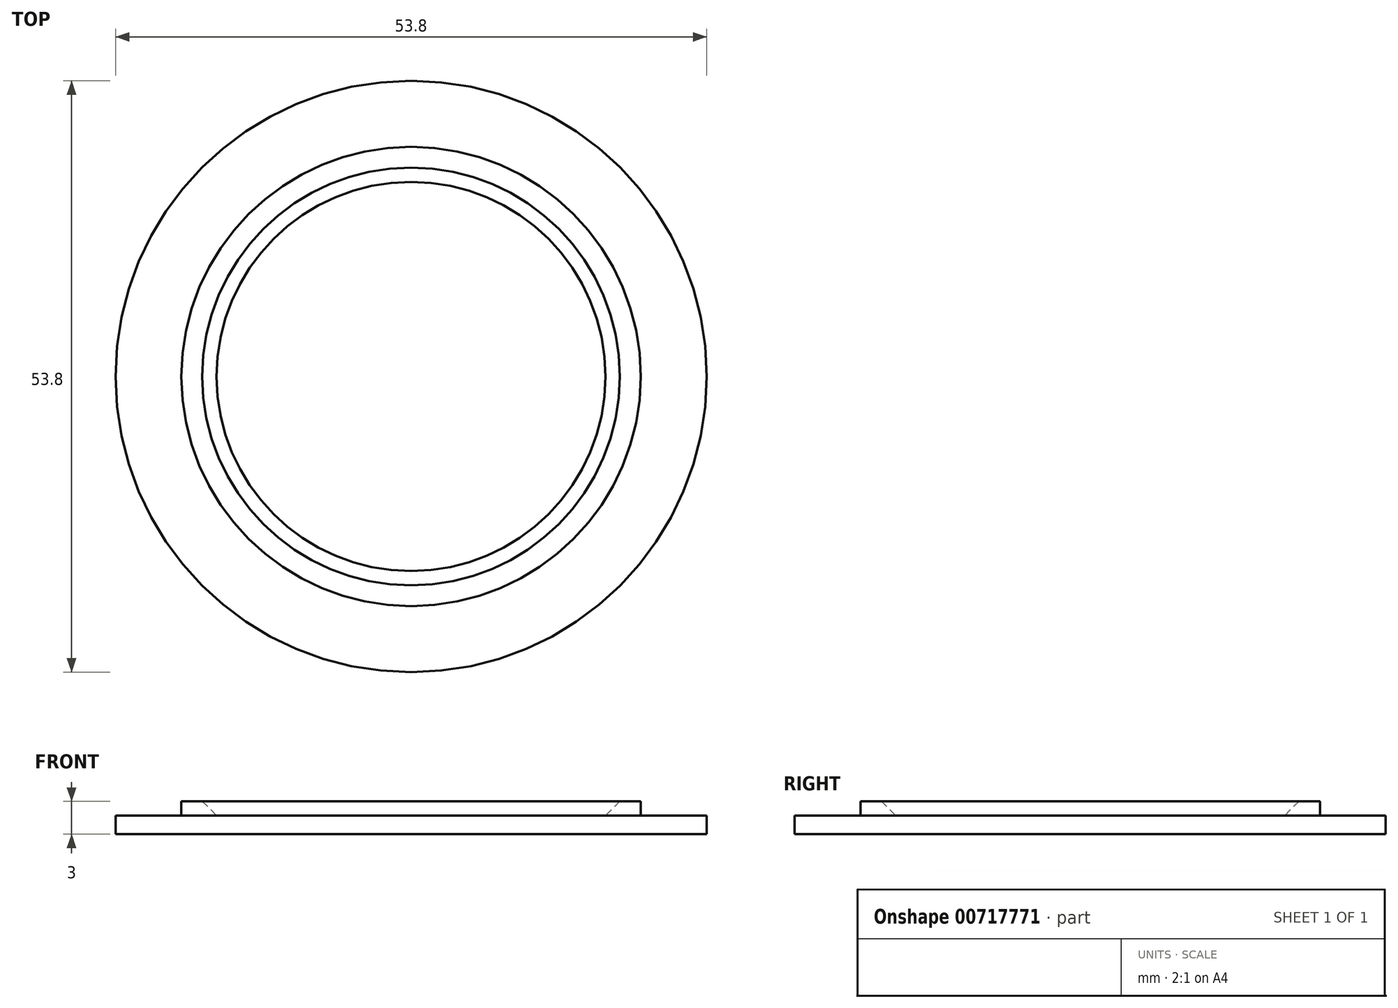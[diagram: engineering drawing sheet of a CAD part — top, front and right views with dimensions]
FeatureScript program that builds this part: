
annotation { "Feature Type Name" : "Feature", "Feature Type Description" : "" }
export const myFeature = defineFeature(function(context is Context, id is Id, definition is map)
    precondition{}
    {
        {
            var Q0;
            Q0=qCreatedBy(makeId("Top.planeOp"),FACE);
            var sketch = newSketch(context, id + "F0", { "sketchPlane" : qUnion([Q0])});
            skCircle(sketch, "E0", {"center": v(0, 0) * mm, "radius": 26.9 * mm});
            skCircle(sketch, "E1", {"center": v(0, 0) * mm, "radius": 20.9 * mm});
            skSolve(sketch);
        }
        {
            var Q0;
            Q0 = qSketchRegion(id + "F0", true);
            extrude(context, id + "F1", {"entities" : qUnion([Q0]), "depth" : 1.7 * mm, "offsetDistance" : 25 * mm});
        }
        {
            var Q0;
            Q0=makeQuery(id+"F0.imprint","IMPRINT",FACE,{"disambiguationData":[TD([[makeQuery(id+"F0.imprint","IMPRINT",EDGE,{"derivedFrom":sQuery(id+"F0.wireOp",EDGE,"E1")}),1.0]])]});
            extrude(context, id + "F2", {"entities" : qUnion([Q0]), "operationType" : NewBodyOperationType.ADD, "depth" : 3 * mm, "offsetDistance" : 25 * mm});
        }
        {
            var Q0;
            Q0=makeQuery(id+"F2.opExtrude","CAP_FACE",FACE,{"disambiguationData":[OSD([sQuery(id+"F0.wireOp",EDGE,"E1")])],"isStart":false});
            var sketch = newSketch(context, id + "F3", { "sketchPlane" : qUnion([Q0])});
            skCircle(sketch, "E2", {"center": v(0, 0) * mm, "radius": 19 * mm});
            skSolve(sketch);
        }
        {
            var Q0;
            Q0=makeQuery(id+"F3.imprint","IMPRINT",FACE,{"disambiguationData":[TD([[makeQuery(id+"F3.imprint","IMPRINT",EDGE,{"derivedFrom":sQuery(id+"F3.wireOp",EDGE,"E2")}),1.0]])]});
            extrude(context, id + "F4", {"entities" : qUnion([Q0]), "operationType" : NewBodyOperationType.REMOVE, "oppositeDirection" : true, "depth" : 1.3 * mm, "offsetDistance" : 25 * mm});
        }
        {
            var Q0;
            Q0=makeQuery(id+"F4.boolean.opBoolean","COPY",EDGE,{"derivedFrom":makeQuery(id+"F4.opExtrude","CAP_EDGE",EDGE,{"disambiguationData":[OSD([sQuery(id+"F3.wireOp",EDGE,"E2")])],"isStart":false})});
            chamfer(context, id + "F5", {"entities" : qUnion([Q0]), "width" : 1.3 * mm, "tangentPropagation" : true});
        }
    });
